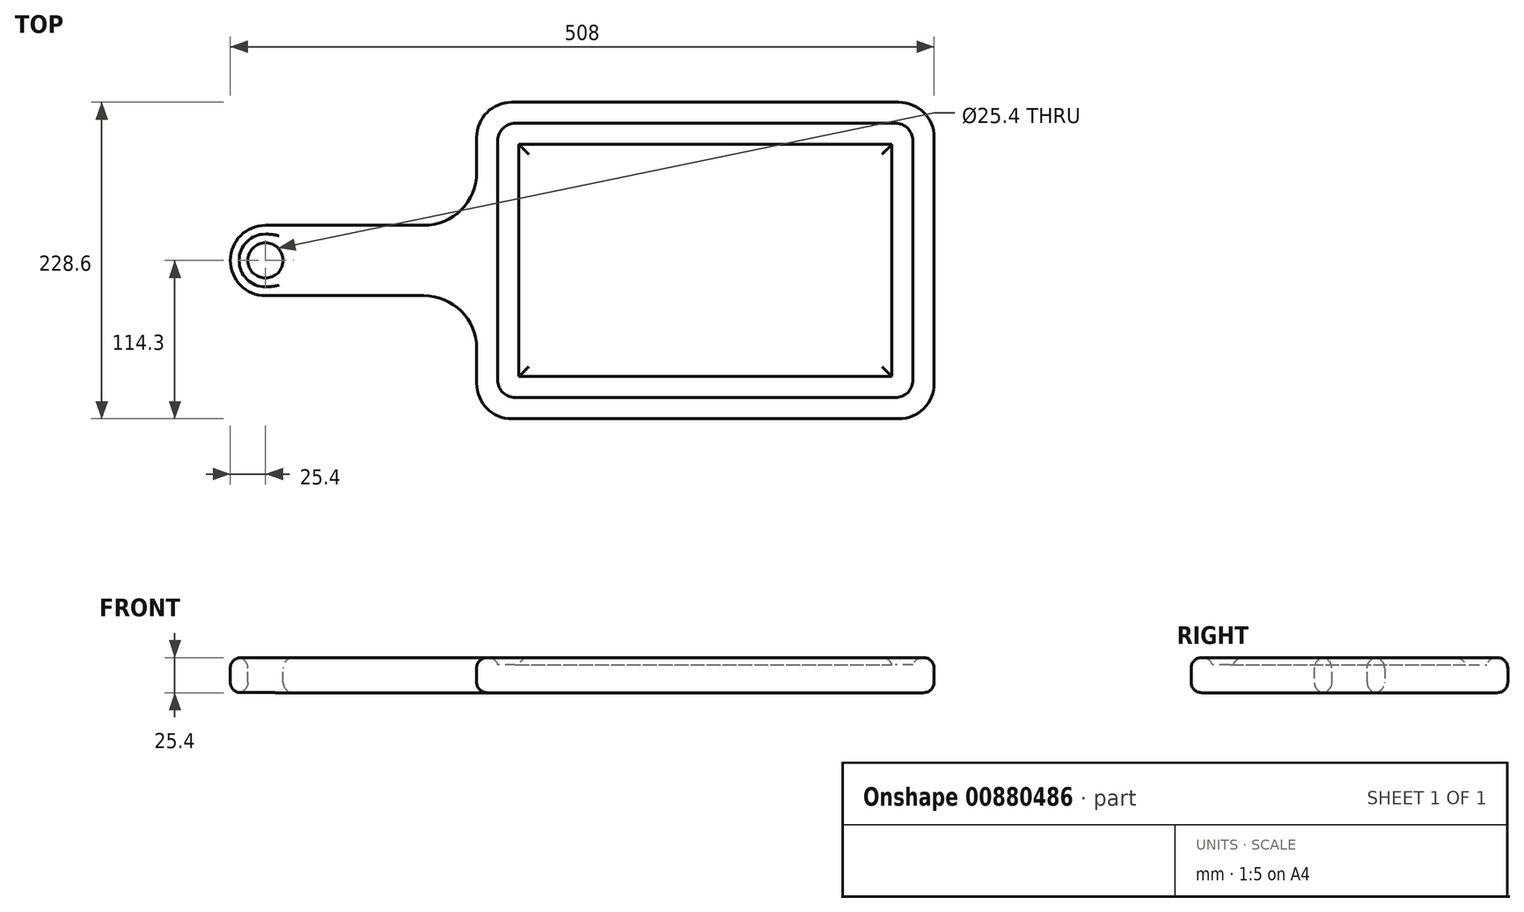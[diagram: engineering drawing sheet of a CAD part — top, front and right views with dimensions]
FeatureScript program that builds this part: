
annotation { "Feature Type Name" : "Feature", "Feature Type Description" : "" }
export const myFeature = defineFeature(function(context is Context, id is Id, definition is map)
    precondition{}
    {
        {
            var Q0;
            Q0=qCreatedBy(makeId("Top.planeOp"),FACE);
            var sketch = newSketch(context, id + "F0", { "sketchPlane" : qUnion([Q0])});
            skLineSegment(sketch, "E0.bottom", {"start": v(0, 0) * mm, "end": v(330.2, 0) * mm});
            skLineSegment(sketch, "E0.top", {"start": v(0, 228.6) * mm, "end": v(330.2, 228.6) * mm});
            skLineSegment(sketch, "E0.left", {"start": v(0, 0) * mm, "end": v(0, 228.6) * mm});
            skLineSegment(sketch, "E0.right", {"start": v(330.2, 0) * mm, "end": v(330.2, 228.6) * mm});
            skLineSegment(sketch, "E1.bottom", {"start": v(0, 139.7) * mm, "end": v(-177.8, 139.7) * mm});
            skLineSegment(sketch, "E1.top", {"start": v(0, 88.9) * mm, "end": v(-177.8, 88.9) * mm});
            skLineSegment(sketch, "E1.left", {"start": v(0, 139.7) * mm, "end": v(0, 88.9) * mm});
            skLineSegment(sketch, "E1.right", {"start": v(-177.8, 139.7) * mm, "end": v(-177.8, 88.9) * mm});
            skSolve(sketch);
        }
        {
            var Q0;
            {var subQ3=sQuery(id+"F0.wireOp",EDGE,"E0.bottom");Q0=makeQuery(id+"F0.imprint","IMPRINT",FACE,{"disambiguationData":[TD([[makeQuery(id+"F0.imprint","IMPRINT",EDGE,{"derivedFrom":subQ3}),1.0]])]});}
            var Q1;
            Q1=makeQuery(id+"F0.imprint","IMPRINT",FACE,{"disambiguationData":[TD([[makeQuery(id+"F0.imprint","IMPRINT",EDGE,{"derivedFrom":sQuery(id+"F0.wireOp",EDGE,"E1.bottom")}),1.0]])]});
            extrude(context, id + "F1", {"entities" : qUnion([Q0, Q1]), "depth" : 25.4 * mm, "offsetDistance" : 25.4 * mm});
        }
        {
            var Q0;
            Q0=makeQuery(id+"F1.opExtrude","CAP_FACE",FACE,{"disambiguationData":[OSD([sQuery(id+"F0.wireOp",EDGE,"E0.bottom"),sQuery(id+"F0.wireOp",EDGE,"E0.top"),sQuery(id+"F0.wireOp",EDGE,"E0.left"),sQuery(id+"F0.wireOp",EDGE,"E0.right"),sQuery(id+"F0.wireOp",EDGE,"E1.bottom"),sQuery(id+"F0.wireOp",EDGE,"E1.top"),sQuery(id+"F0.wireOp",EDGE,"E1.right")])],"isStart":false});
            var sketch = newSketch(context, id + "F2", { "sketchPlane" : qUnion([Q0])});
            skCircle(sketch, "E2", {"center": v(-152.4, 114.3) * mm, "radius": 12.7 * mm});
            skSolve(sketch);
        }
        {
            var Q0;
            Q0 = qSketchRegion(id + "F2", true);
            extrude(context, id + "F3", {"entities" : qUnion([Q0]), "operationType" : NewBodyOperationType.REMOVE, "oppositeDirection" : true, "depth" : 25.4 * mm, "offsetDistance" : 25.4 * mm});
        }
        {
            var Q0;
            Q0=makeQuery(id+"F1.opExtrude","CAP_FACE",FACE,{"disambiguationData":[OSD([sQuery(id+"F0.wireOp",EDGE,"E0.bottom"),sQuery(id+"F0.wireOp",EDGE,"E0.top"),sQuery(id+"F0.wireOp",EDGE,"E0.left"),sQuery(id+"F0.wireOp",EDGE,"E0.right"),sQuery(id+"F0.wireOp",EDGE,"E1.bottom"),sQuery(id+"F0.wireOp",EDGE,"E1.top"),sQuery(id+"F0.wireOp",EDGE,"E1.right")])],"isStart":false});
            var sketch = newSketch(context, id + "F4", { "sketchPlane" : qUnion([Q0])});
            skLineSegment(sketch, "E3.0", {"start": v(15.24, 15.24) * mm, "end": v(15.24, 88.9) * mm});
            skLineSegment(sketch, "E3.1", {"start": v(15.24, 139.7) * mm, "end": v(15.24, 213.36) * mm});
            skLineSegment(sketch, "E3.2", {"start": v(15.24, 213.36) * mm, "end": v(314.96, 213.36) * mm});
            skLineSegment(sketch, "E3.3", {"start": v(314.96, 15.24) * mm, "end": v(314.96, 213.36) * mm});
            skLineSegment(sketch, "E3.4", {"start": v(15.24, 15.24) * mm, "end": v(314.96, 15.24) * mm});
            skLineSegment(sketch, "E4", {"start": v(15.24, 139.7) * mm, "end": v(15.24, 88.9) * mm});
            skLineSegment(sketch, "E5.0", {"start": v(30.48, 139.7) * mm, "end": v(30.48, 198.12) * mm});
            skLineSegment(sketch, "E5.1", {"start": v(299.72, 30.48) * mm, "end": v(299.72, 198.12) * mm});
            skLineSegment(sketch, "E5.2", {"start": v(30.48, 30.48) * mm, "end": v(299.72, 30.48) * mm});
            skLineSegment(sketch, "E5.3", {"start": v(30.48, 198.12) * mm, "end": v(299.72, 198.12) * mm});
            skLineSegment(sketch, "E5.4", {"start": v(30.48, 30.48) * mm, "end": v(30.48, 88.9) * mm});
            skLineSegment(sketch, "E5.5", {"start": v(30.48, 139.7) * mm, "end": v(30.48, 88.9) * mm});
            skSolve(sketch);
        }
        {
            var Q0;
            Q0=makeQuery(id+"F4.imprint","IMPRINT",FACE,{"disambiguationData":[TD([[makeQuery(id+"F4.imprint","IMPRINT",EDGE,{"derivedFrom":sQuery(id+"F4.wireOp",EDGE,"E3.0")}),-1.0]])]});
            extrude(context, id + "F5", {"entities" : qUnion([Q0]), "operationType" : NewBodyOperationType.REMOVE, "oppositeDirection" : true, "depth" : 5.08 * mm, "offsetDistance" : 25.4 * mm});
        }
        {
            var Q0;
            Q0=makeQuery(id+"F5.boolean.opBoolean","COPY",EDGE,{"derivedFrom":makeQuery(id+"F5.opExtrude","SWEPT_EDGE",EDGE,{"disambiguationData":[OSD([sQuery(id+"F4.wireOp",EDGE,"E3.1"),sQuery(id+"F4.wireOp",EDGE,"E3.2")])]})});
            var Q1;
            Q1=makeQuery(id+"F5.boolean.opBoolean","COPY",EDGE,{"derivedFrom":makeQuery(id+"F5.opExtrude","SWEPT_EDGE",EDGE,{"disambiguationData":[OSD([sQuery(id+"F4.wireOp",EDGE,"E3.0"),sQuery(id+"F4.wireOp",EDGE,"E3.4")])]})});
            var Q2;
            Q2=makeQuery(id+"F5.boolean.opBoolean","COPY",EDGE,{"derivedFrom":makeQuery(id+"F5.opExtrude","SWEPT_EDGE",EDGE,{"disambiguationData":[OSD([sQuery(id+"F4.wireOp",EDGE,"E3.3"),sQuery(id+"F4.wireOp",EDGE,"E3.4")])]})});
            var Q3;
            Q3=makeQuery(id+"F5.boolean.opBoolean","COPY",EDGE,{"derivedFrom":makeQuery(id+"F5.opExtrude","SWEPT_EDGE",EDGE,{"disambiguationData":[OSD([sQuery(id+"F4.wireOp",EDGE,"E3.2"),sQuery(id+"F4.wireOp",EDGE,"E3.3")])]})});
            fillet(context, id + "F6", {"entities" : qUnion([Q0, Q1, Q2, Q3]), "radius" : 12.7 * mm, "tangentPropagation" : true, "allowEdgeOverflow" : false});
        }
        {
            var Q0;
            Q0=makeQuery(id+"F1.opExtrude","SWEPT_EDGE",EDGE,{"disambiguationData":[OSD([sQuery(id+"F0.wireOp",EDGE,"E1.top"),sQuery(id+"F0.wireOp",EDGE,"E1.right")])]});
            var Q1;
            Q1=makeQuery(id+"F1.opExtrude","SWEPT_EDGE",EDGE,{"disambiguationData":[OSD([sQuery(id+"F0.wireOp",EDGE,"E1.bottom"),sQuery(id+"F0.wireOp",EDGE,"E1.right")])]});
            var Q2;
            Q2=makeQuery(id+"F1.opExtrude","SWEPT_EDGE",EDGE,{"disambiguationData":[OSD([sQuery(id+"F0.wireOp",EDGE,"E0.bottom"),sQuery(id+"F0.wireOp",EDGE,"E0.left")])]});
            var Q3;
            Q3=makeQuery(id+"F1.opExtrude","SWEPT_EDGE",EDGE,{"disambiguationData":[OSD([sQuery(id+"F0.wireOp",EDGE,"E0.bottom"),sQuery(id+"F0.wireOp",EDGE,"E0.right")])]});
            var Q4;
            Q4=makeQuery(id+"F1.opExtrude","SWEPT_EDGE",EDGE,{"disambiguationData":[OSD([sQuery(id+"F0.wireOp",EDGE,"E0.top"),sQuery(id+"F0.wireOp",EDGE,"E0.right")])]});
            var Q5;
            Q5=makeQuery(id+"F1.opExtrude","SWEPT_EDGE",EDGE,{"disambiguationData":[OSD([sQuery(id+"F0.wireOp",EDGE,"E0.top"),sQuery(id+"F0.wireOp",EDGE,"E0.left")])]});
            fillet(context, id + "F7", {"entities" : qUnion([Q0, Q1, Q2, Q3, Q4, Q5]), "radius" : 25.4 * mm, "tangentPropagation" : true, "allowEdgeOverflow" : false});
        }
        {
            var Q0;
            Q0=makeQuery(id+"F1.opExtrude","SWEPT_EDGE",EDGE,{"disambiguationData":[OSD([sQuery(id+"F0.wireOp",EDGE,"E0.left"),sQuery(id+"F0.wireOp",EDGE,"E1.top"),sQuery(id+"F0.wireOp",EDGE,"E1.left")])]});
            var Q1;
            Q1=makeQuery(id+"F1.opExtrude","SWEPT_EDGE",EDGE,{"disambiguationData":[OSD([sQuery(id+"F0.wireOp",EDGE,"E0.left"),sQuery(id+"F0.wireOp",EDGE,"E1.bottom"),sQuery(id+"F0.wireOp",EDGE,"E1.left")])]});
            fillet(context, id + "F8", {"entities" : qUnion([Q0, Q1]), "radius" : 38.1 * mm, "tangentPropagation" : true, "allowEdgeOverflow" : false});
        }
        {
            var Q0;
            Q0=makeQuery(id+"F1.opExtrude","CAP_FACE",FACE,{"disambiguationData":[OSD([sQuery(id+"F0.wireOp",EDGE,"E0.bottom"),sQuery(id+"F0.wireOp",EDGE,"E0.top"),sQuery(id+"F0.wireOp",EDGE,"E0.left"),sQuery(id+"F0.wireOp",EDGE,"E0.right"),sQuery(id+"F0.wireOp",EDGE,"E1.bottom"),sQuery(id+"F0.wireOp",EDGE,"E1.top"),sQuery(id+"F0.wireOp",EDGE,"E1.right")])],"isStart":true});
            var Q1;
            Q1=makeQuery(id+"F5.boolean.opBoolean","SPLIT",FACE,{"disambiguationData":[TD([makeQuery(id+"F5.opExtrude","SWEPT_FACE",FACE,{"disambiguationData":[OSD([sQuery(id+"F4.wireOp",EDGE,"E5.1")])]})])],"derivedFrom":makeQuery(id+"F1.opExtrude","CAP_FACE",FACE,{"disambiguationData":[OSD([sQuery(id+"F0.wireOp",EDGE,"E0.bottom"),sQuery(id+"F0.wireOp",EDGE,"E0.top"),sQuery(id+"F0.wireOp",EDGE,"E0.left"),sQuery(id+"F0.wireOp",EDGE,"E0.right"),sQuery(id+"F0.wireOp",EDGE,"E1.bottom"),sQuery(id+"F0.wireOp",EDGE,"E1.top"),sQuery(id+"F0.wireOp",EDGE,"E1.right")])],"isStart":false})});
            var Q2;
            {var subQ0=sQuery(id+"F0.wireOp",EDGE,"E1.right");var subQ1=sQuery(id+"F0.wireOp",EDGE,"E1.top");var subQ2=sQuery(id+"F0.wireOp",EDGE,"E1.bottom");var subQ3=sQuery(id+"F0.wireOp",EDGE,"E0.right");var subQ4=sQuery(id+"F0.wireOp",EDGE,"E0.bottom");var subQ5=sQuery(id+"F0.wireOp",EDGE,"E0.left");var subQ6=sQuery(id+"F0.wireOp",EDGE,"E0.top");Q2=makeQuery(id+"F5.boolean.opBoolean","SPLIT",FACE,{"disambiguationData":[TD([makeQuery(id+"F1.opExtrude","SWEPT_FACE",FACE,{"disambiguationData":[OSD([subQ4])]})])],"derivedFrom":makeQuery(id+"F1.opExtrude","CAP_FACE",FACE,{"disambiguationData":[OSD([subQ4,subQ6,subQ5,subQ3,subQ2,subQ1,subQ0])],"isStart":false})});}
            fillet(context, id + "F9", {"entities" : qUnion([Q0, Q1, Q2]), "radius" : 7.62 * mm, "tangentPropagation" : true, "allowEdgeOverflow" : false});
        }
    });
